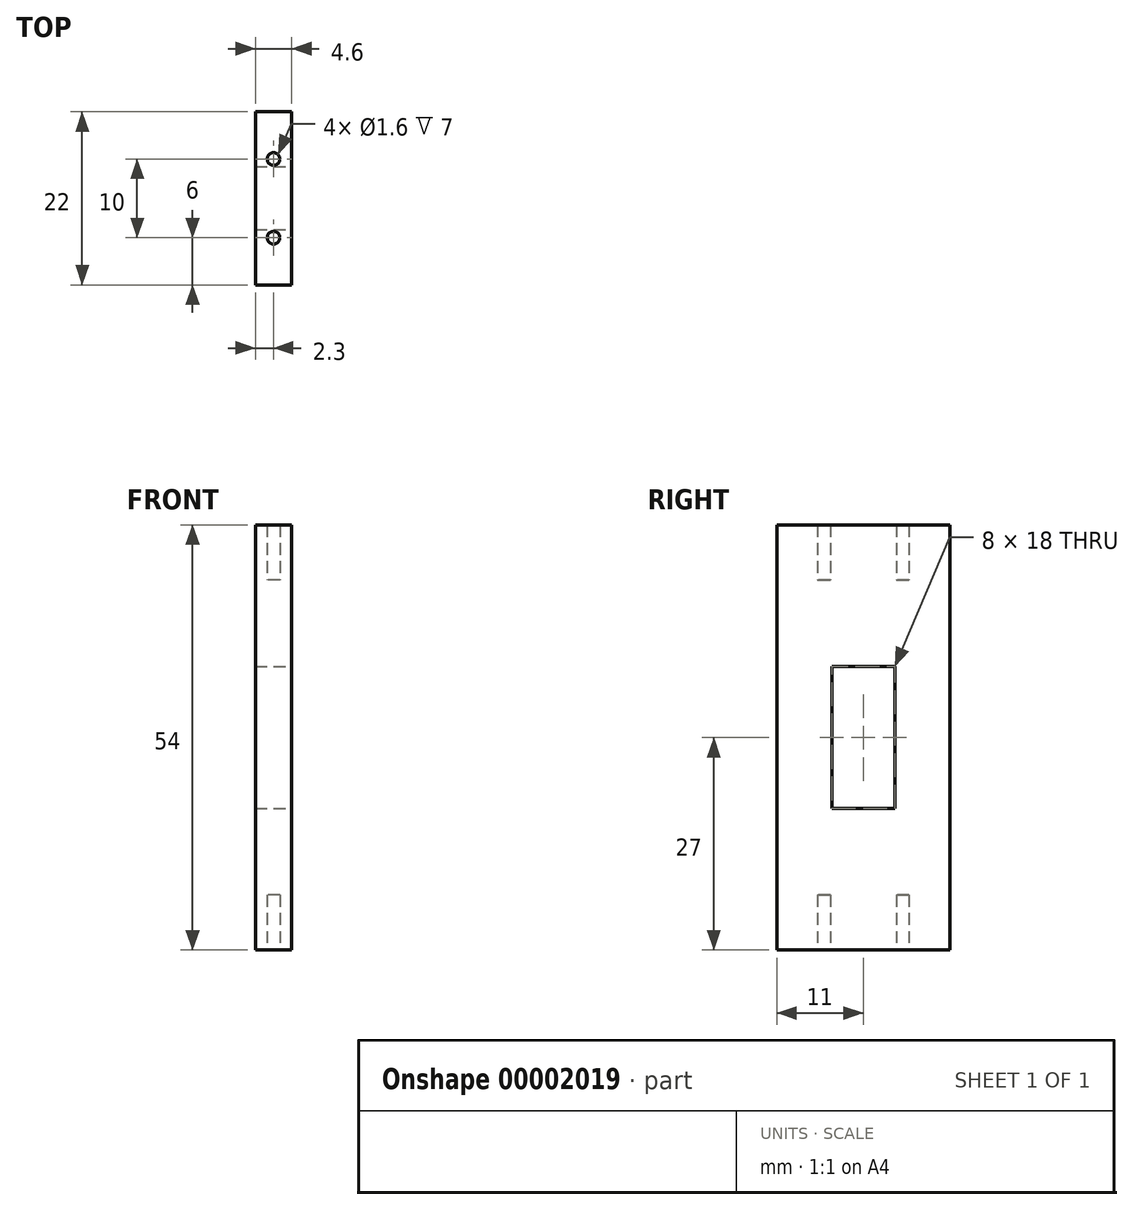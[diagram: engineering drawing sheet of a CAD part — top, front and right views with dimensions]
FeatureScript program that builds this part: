
annotation { "Feature Type Name" : "Feature", "Feature Type Description" : "" }
export const myFeature = defineFeature(function(context is Context, id is Id, definition is map)
    precondition{}
    {
        {
            var Q0;
            Q0=qCreatedBy(makeId("Top.planeOp"),FACE);
            var sketch = newSketch(context, id + "F0", { "sketchPlane" : qUnion([Q0])});
            skLineSegment(sketch, "E0.rect.bottom", {"start": v(2.3, 11) * mm, "end": v(-2.3, 11) * mm});
            skLineSegment(sketch, "E0.rect.top", {"start": v(2.3, -11) * mm, "end": v(-2.3, -11) * mm});
            skLineSegment(sketch, "E0.rect.left", {"start": v(2.3, 11) * mm, "end": v(2.3, -11) * mm});
            skLineSegment(sketch, "E0.rect.right", {"start": v(-2.3, 11) * mm, "end": v(-2.3, -11) * mm});
            skPoint(sketch, "E0.rect.middle", {"position": v(0, 0) * mm});
            skCircle(sketch, "E1", {"center": v(0, 5) * mm, "radius": 0.8 * mm});
            skCircle(sketch, "E2", {"center": v(0, -5) * mm, "radius": 0.8 * mm});
            skSolve(sketch);
        }
        {
            var Q0;
            Q0=makeQuery(id+"F0.imprint","IMPRINT",FACE,{"disambiguationData":[TD([[makeQuery(id+"F0.imprint","IMPRINT",EDGE,{"derivedFrom":sQuery(id+"F0.wireOp",EDGE,"E0.rect.bottom")}),1.0]])]});
            extrude(context, id + "F1", {"entities" : qUnion([Q0]), "endBound" : BoundingType.SYMMETRIC, "depth" : (27 * 2) * mm});
        }
        {
            var Q0;
            Q0=makeQuery(id+"F0.imprint","IMPRINT",FACE,{"disambiguationData":[TD([[makeQuery(id+"F0.imprint","IMPRINT",EDGE,{"derivedFrom":sQuery(id+"F0.wireOp",EDGE,"E1")}),1.0]])]});
            var Q1;
            Q1=makeQuery(id+"F0.imprint","IMPRINT",FACE,{"disambiguationData":[TD([[makeQuery(id+"F0.imprint","IMPRINT",EDGE,{"derivedFrom":sQuery(id+"F0.wireOp",EDGE,"E2")}),1.0]])]});
            extrude(context, id + "F2", {"entities" : qUnion([Q0, Q1]), "operationType" : NewBodyOperationType.ADD, "endBound" : BoundingType.SYMMETRIC, "depth" : 40 * mm});
        }
        {
            var Q0;
            Q0=makeQuery(id+"F1.opExtrude","SWEPT_FACE",FACE,{"disambiguationData":[OSD([sQuery(id+"F0.wireOp",EDGE,"E0.rect.left")])]});
            var sketch = newSketch(context, id + "F3", { "sketchPlane" : qUnion([Q0])});
            skLineSegment(sketch, "E3.rect.bottom", {"start": v(4, -9) * mm, "end": v(-4, -9) * mm});
            skLineSegment(sketch, "E3.rect.top", {"start": v(4, 9) * mm, "end": v(-4, 9) * mm});
            skLineSegment(sketch, "E3.rect.left", {"start": v(4, -9) * mm, "end": v(4, 9) * mm});
            skLineSegment(sketch, "E3.rect.right", {"start": v(-4, -9) * mm, "end": v(-4, 9) * mm});
            skPoint(sketch, "E3.rect.middle", {"position": v(0, 0) * mm});
            skSolve(sketch);
        }
        {
            var Q0;
            Q0=makeQuery(id+"F3.imprint","IMPRINT",FACE,{"disambiguationData":[TD([[makeQuery(id+"F3.imprint","IMPRINT",EDGE,{"derivedFrom":sQuery(id+"F3.wireOp",EDGE,"E3.rect.bottom")}),-1.0]])]});
            extrude(context, id + "F4", {"entities" : qUnion([Q0]), "operationType" : NewBodyOperationType.REMOVE, "endBound" : BoundingType.THROUGH_ALL, "oppositeDirection" : true, "depth" : 25 * mm});
        }
    });
